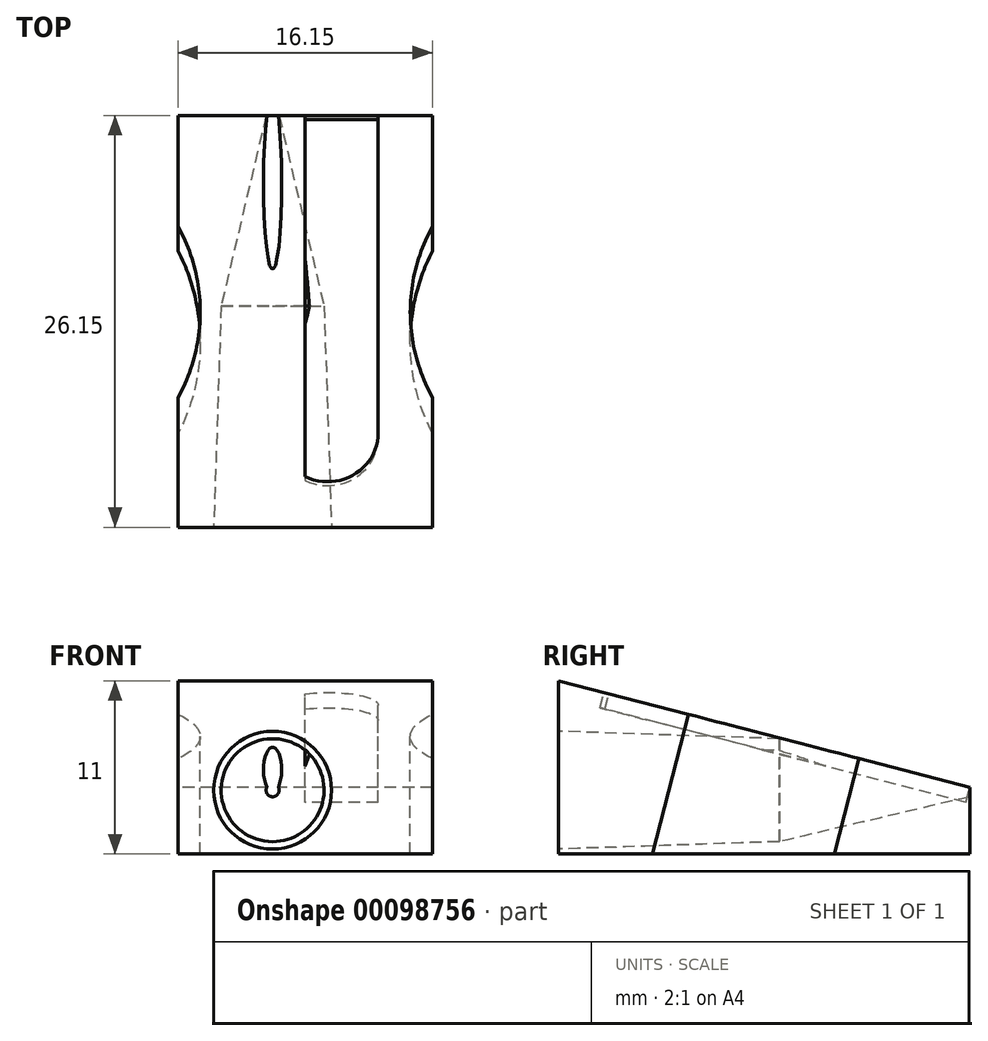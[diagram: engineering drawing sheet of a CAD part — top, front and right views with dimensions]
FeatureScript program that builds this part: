
annotation { "Feature Type Name" : "Feature", "Feature Type Description" : "" }
export const myFeature = defineFeature(function(context is Context, id is Id, definition is map)
    precondition{}
    {
        {
            var Q0;
            Q0=qCreatedBy(makeId("Right.planeOp"),FACE);
            var sketch = newSketch(context, id + "F0", { "sketchPlane" : qUnion([Q0])});
            skLineSegment(sketch, "E0", {"start": v(19.75, -11) * mm, "end": v(-6.4, -11) * mm});
            skLineSegment(sketch, "E1", {"start": v(19.75, -11) * mm, "end": v(19.75, 0) * mm});
            skLineSegment(sketch, "E2", {"start": v(-6.4, -11) * mm, "end": v(-6.4, 0) * mm});
            skLineSegment(sketch, "E3", {"start": v(19.75, 0) * mm, "end": v(-6.4, 0) * mm});
            skSolve(sketch);
        }
        {
            var Q0;
            Q0 = qSketchRegion(id + "F0", true);
            extrude(context, id + "F1", {"entities" : qUnion([Q0]), "depth" : 16.15 * mm});
        }
        {
            var Q0;
            Q0=makeQuery(id+"F1.opExtrude","CAP_FACE",FACE,{"disambiguationData":[OSD([sQuery(id+"F0.wireOp",EDGE,"E0"),sQuery(id+"F0.wireOp",EDGE,"E1"),sQuery(id+"F0.wireOp",EDGE,"E2"),sQuery(id+"F0.wireOp",EDGE,"E3")])],"isStart":true});
            var sketch = newSketch(context, id + "F2", { "sketchPlane" : qUnion([Q0])});
            skLineSegment(sketch, "E4", {"start": v(6.4, 0) * mm, "end": v(-19.75, -6.76) * mm});
            skSolve(sketch);
        }
        {
            var Q0;
            {var subQ0=sQuery(id+"F2.wireOp",EDGE,"E4");Q0=makeQuery(id+"F2.imprint","IMPRINT",FACE,{"disambiguationData":[TD([[makeQuery(id+"F2.imprint","IMPRINT",EDGE,{"derivedFrom":subQ0}),-1.0]])]});}
            extrude(context, id + "F3", {"entities" : qUnion([Q0]), "operationType" : NewBodyOperationType.REMOVE, "oppositeDirection" : true, "depth" : 25 * mm});
        }
        {
            var Q0;
            Q0=makeQuery(id+"F3.boolean.opBoolean","COPY",FACE,{"derivedFrom":makeQuery(id+"F3.opExtrude","SWEPT_FACE",FACE,{"disambiguationData":[OSD([sQuery(id+"F2.wireOp",EDGE,"E4")])]})});
            var sketch = newSketch(context, id + "F4", { "sketchPlane" : qUnion([Q0])});
            skLineSegment(sketch, "E5", {"start": v(12.71, 20.8) * mm, "end": v(12.71, 0) * mm});
            skLineSegment(sketch, "E6", {"start": v(6.3, 20.8) * mm, "end": v(6.3, 0) * mm});
            skArc(sketch, "E7", {"start": v(6.3, 0) * mm, "mid": v(9.5, -3.2) * mm, "end": v(12.71, 0) * mm});
            skLineSegment(sketch, "E8", {"start": v(8.07, 20.8) * mm, "end": v(8.07, -2.88) * mm});
            skSolve(sketch);
        }
        {
            var Q0;
            {var subQ0=sQuery(id+"F4.wireOp",EDGE,"E5");Q0=makeQuery(id+"F4.imprint","IMPRINT",FACE,{"disambiguationData":[TD([[makeQuery(id+"F4.imprint","IMPRINT",EDGE,{"derivedFrom":subQ0}),-1.0]])]});}
            extrude(context, id + "F5", {"entities" : qUnion([Q0]), "operationType" : NewBodyOperationType.REMOVE, "oppositeDirection" : true, "depth" : 1 * mm});
        }
        {
            var Q0;
            Q0=makeQuery(id+"F5.boolean.opBoolean","COPY",FACE,{"derivedFrom":makeQuery(id+"F5.opExtrude","CAP_FACE",FACE,{"disambiguationData":[OSD([sQuery(id+"F0.wireOp",EDGE,"E1"),sQuery(id+"F2.wireOp",EDGE,"E4"),sQuery(id+"F4.wireOp",EDGE,"E5"),sQuery(id+"F4.wireOp",EDGE,"E7"),sQuery(id+"F4.wireOp",EDGE,"E8")])],"isStart":false})});
            var sketch = newSketch(context, id + "F6", { "sketchPlane" : qUnion([Q0])});
            skCircle(sketch, "E9", {"center": v(10.36, 9.88) * mm, "radius": 1.44 * mm});
            skSolve(sketch);
        }
        {
            var Q0;
            Q0=sQuery(id+"F6.wireOp",EDGE,"E9");
            extrude(context, id + "F7", {"bodyType" : ToolBodyType.SURFACE, "surfaceEntities" : qUnion([Q0]), "depth" : 1 * mm});
        }
        {
            var Q0;
            Q0=qCreatedBy(makeId("Right.planeOp"),FACE);
            cPlane(context, id + "F8", {"entities" : qUnion([Q0]), "cplaneType" : CPlaneType.OFFSET, "offset" : 6 * mm, "width" : 150 * mm, "height" : 150 * mm});
        }
        {
            var Q0;
            Q0=qCreatedBy(id+"F8.planeOp",FACE);
            var sketch = newSketch(context, id + "F9", { "sketchPlane" : qUnion([Q0])});
            skLineSegment(sketch, "E10", {"start": v(-6.72, -3.2) * mm, "end": v(7.64, -3.68) * mm});
            skLineSegment(sketch, "E11", {"start": v(7.64, -3.68) * mm, "end": v(7.64, -6.95) * mm});
            skLineSegment(sketch, "E12", {"start": v(7.64, -6.95) * mm, "end": v(-6.72, -6.95) * mm});
            skLineSegment(sketch, "E13", {"start": v(-6.72, -6.95) * mm, "end": v(-6.72, -3.2) * mm});
            skLineSegment(sketch, "E14", {"start": v(7.64, -3.68) * mm, "end": v(19.83, -6.56) * mm});
            skLineSegment(sketch, "E15", {"start": v(7.64, -6.95) * mm, "end": v(19.83, -6.95) * mm});
            skLineSegment(sketch, "E16", {"start": v(19.83, -6.56) * mm, "end": v(19.83, -6.95) * mm});
            skSolve(sketch);
        }
        {
            var Q0;
            Q0 = qSketchRegion(id + "F9", true);
            var Q1;
            Q1=sQuery(id+"F9.wireOp",EDGE,"E12");
            revolve(context, id + "F10", {"operationType" : NewBodyOperationType.REMOVE, "entities" : qUnion([Q0]), "axis" : qUnion([Q1]), "revolveType" : RevolveType.FULL, "oppositeDirection" : true});
        }
        {
            var Q0;
            Q0=makeQuery(id+"F9.imprint","IMPRINT",FACE,{"disambiguationData":[TD([[makeQuery(id+"F9.imprint","IMPRINT",EDGE,{"derivedFrom":sQuery(id+"F9.wireOp",EDGE,"E11")}),1.0]])]});
            var Q1;
            Q1=sQuery(id+"F9.wireOp",EDGE,"E15");
            revolve(context, id + "F11", {"operationType" : NewBodyOperationType.REMOVE, "entities" : qUnion([Q0]), "axis" : qUnion([Q1]), "revolveType" : RevolveType.FULL, "oppositeDirection" : true});
        }
        {
            var Q0;
            {var subQ1=sQuery(id+"F4.wireOp",EDGE,"E5");Q0=makeQuery(id+"F4.imprint","IMPRINT",FACE,{"disambiguationData":[TD([[makeQuery(id+"F4.imprint","IMPRINT",EDGE,{"derivedFrom":subQ1}),1.0]])]});}
            var sketch = newSketch(context, id + "F12", { "sketchPlane" : qUnion([Q0])});
            skArc(sketch, "E17", {"start": v(0, 2.33) * mm, "mid": v(1.4, 7.93) * mm, "end": v(0, 13.54) * mm});
            skLineSegment(sketch, "E18", {"start": v(0, 13.54) * mm, "end": v(0, 2.33) * mm});
            skArc(sketch, "E19", {"start": v(16.15, 13.54) * mm, "mid": v(14.74, 7.93) * mm, "end": v(16.15, 2.33) * mm});
            skLineSegment(sketch, "E20", {"start": v(16.15, 13.54) * mm, "end": v(16.15, 2.33) * mm});
            skSolve(sketch);
        }
        {
            var Q0;
            Q0 = qSketchRegion(id + "F12", true);
            extrude(context, id + "F13", {"entities" : qUnion([Q0]), "operationType" : NewBodyOperationType.REMOVE, "oppositeDirection" : true, "depth" : 10 * mm});
        }
    });
